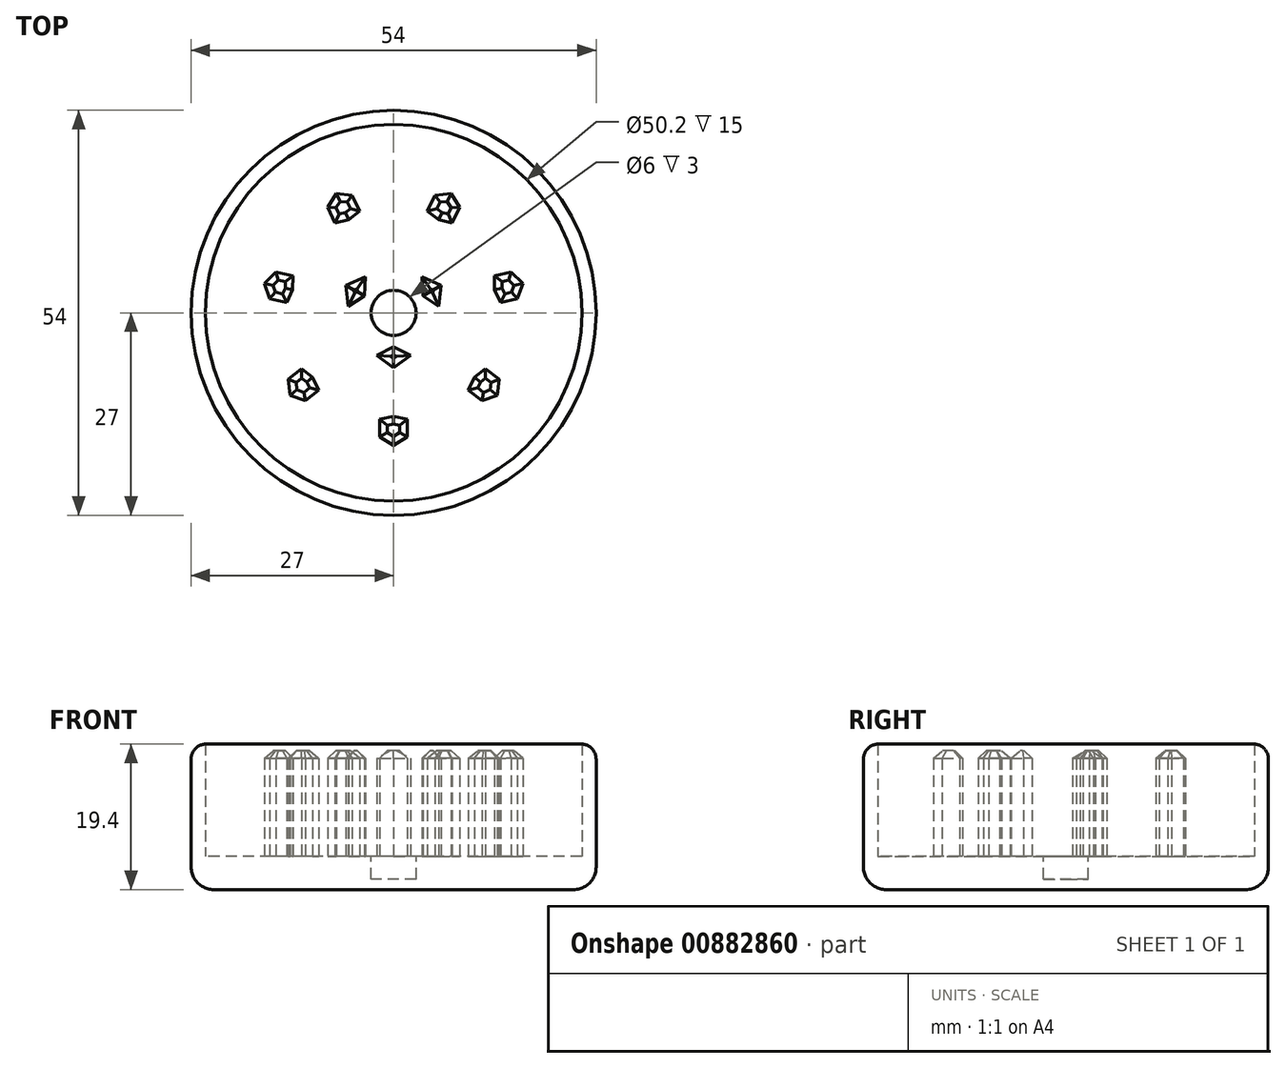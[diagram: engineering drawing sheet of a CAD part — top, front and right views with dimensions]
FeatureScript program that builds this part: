
annotation { "Feature Type Name" : "Feature", "Feature Type Description" : "" }
export const myFeature = defineFeature(function(context is Context, id is Id, definition is map)
    precondition{}
    {
        {
            var Q0;
            Q0=qCreatedBy(makeId("Top.planeOp"),FACE);
            var sketch = newSketch(context, id + "F0", { "sketchPlane" : qUnion([Q0])});
            skCircle(sketch, "E0", {"center": v(0, 0) * mm, "radius": 25 * mm});
            skCircle(sketch, "E1", {"center": v(0, 0) * mm, "radius": 27 * mm});
            skSolve(sketch);
        }
        {
            var Q0;
            Q0=makeQuery(id+"F0.imprint","IMPRINT",FACE,{"disambiguationData":[TD([[makeQuery(id+"F0.imprint","IMPRINT",EDGE,{"derivedFrom":sQuery(id+"F0.wireOp",EDGE,"E0")}),1.0]])]});
            extrude(context, id + "F1", {"entities" : qUnion([Q0]), "depth" : 4 * mm, "offsetDistance" : 25 * mm});
        }
        {
            var Q0;
            Q0=makeQuery(id+"F1.opExtrude","CAP_FACE",FACE,{"disambiguationData":[OSD([sQuery(id+"F0.wireOp",EDGE,"E0")])],"isStart":false});
            var sketch = newSketch(context, id + "F2", { "sketchPlane" : qUnion([Q0])});
            skCircle(sketch, "E2", {"center": v(0, 0) * mm, "radius": 25 * mm});
            skCircle(sketch, "E3", {"center": v(0, 0) * mm, "radius": 22 * mm});
            skCircle(sketch, "E4", {"center": v(0, 0) * mm, "radius": 4 * mm});
            skCircle(sketch, "E5", {"center": v(0, 0) * mm, "radius": 8 * mm});
            skCircle(sketch, "E6", {"center": v(0, 0) * mm, "radius": 13 * mm});
            skCircle(sketch, "E7", {"center": v(0, 0) * mm, "radius": 18 * mm});
            skLineSegment(sketch, "E8", {"start": v(0, 0) * mm, "end": v(0, -4) * mm});
            skLineSegment(sketch, "E9", {"start": v(0, -4) * mm, "end": v(4, 0) * mm});
            skLineSegment(sketch, "E10", {"start": v(4, 0) * mm, "end": v(0, 4) * mm});
            skLineSegment(sketch, "E11", {"start": v(0, 4) * mm, "end": v(-4, 0) * mm});
            skLineSegment(sketch, "E12", {"start": v(-4, 0) * mm, "end": v(0, -4) * mm});
            skLineSegment(sketch, "E13", {"start": v(0, -13) * mm, "end": v(-2.26, -10.11) * mm});
            skLineSegment(sketch, "E14", {"start": v(1.98, -10.11) * mm, "end": v(0, -13) * mm});
            skLineSegment(sketch, "E15", {"start": v(0, 18) * mm, "end": v(2.55, 21.85) * mm});
            skLineSegment(sketch, "E16", {"start": v(0, 18) * mm, "end": v(-2.55, 21.85) * mm});
            skLineSegment(sketch, "E17.1.0", {"start": v(-14.07, 11.22) * mm, "end": v(-18.67, 11.63) * mm});
            skLineSegment(sketch, "E17.1.1", {"start": v(-14.07, 11.22) * mm, "end": v(-15.5, 15.62) * mm});
            skLineSegment(sketch, "E17.2.0", {"start": v(-17.55, -4) * mm, "end": v(-20.74, -7.35) * mm});
            skLineSegment(sketch, "E17.2.1", {"start": v(-17.55, -4) * mm, "end": v(-21.87, -2.38) * mm});
            skLineSegment(sketch, "E17.3.0", {"start": v(-7.8, -16.22) * mm, "end": v(-7.19, -20.8) * mm});
            skLineSegment(sketch, "E17.3.1", {"start": v(-7.8, -16.22) * mm, "end": v(-11.78, -18.58) * mm});
            skLineSegment(sketch, "E17.4.0", {"start": v(7.8, -16.22) * mm, "end": v(11.78, -18.58) * mm});
            skLineSegment(sketch, "E17.4.1", {"start": v(7.8, -16.22) * mm, "end": v(7.19, -20.8) * mm});
            skLineSegment(sketch, "E17.5.0", {"start": v(17.55, -4) * mm, "end": v(21.87, -2.38) * mm});
            skLineSegment(sketch, "E17.5.1", {"start": v(17.55, -4) * mm, "end": v(20.74, -7.35) * mm});
            skLineSegment(sketch, "E17.6.0", {"start": v(14.07, 11.22) * mm, "end": v(15.5, 15.62) * mm});
            skLineSegment(sketch, "E17.6.1", {"start": v(14.07, 11.22) * mm, "end": v(18.67, 11.63) * mm});
            skLineSegment(sketch, "E18.1.0", {"start": v(10.11, -2.26) * mm, "end": v(8, 0) * mm});
            skLineSegment(sketch, "E18.1.2", {"start": v(8, 0) * mm, "end": v(10.11, 1.98) * mm});
            skLineSegment(sketch, "E18.2.0", {"start": v(2.26, 10.11) * mm, "end": v(0, 8) * mm});
            skLineSegment(sketch, "E18.2.1", {"start": v(-1.98, 10.11) * mm, "end": v(0, 13) * mm});
            skLineSegment(sketch, "E18.3.2", {"start": v(-8, 0) * mm, "end": v(-10.11, -1.98) * mm});
            skLineSegment(sketch, "E18.3.3", {"start": v(-13, 0) * mm, "end": v(-10.11, 2.26) * mm});
            skLineSegment(sketch, "E19", {"start": v(0, -13) * mm, "end": v(0, -13.8) * mm});
            skLineSegment(sketch, "E20", {"start": v(0, -13.8) * mm, "end": v(1.83, -14.2) * mm});
            skLineSegment(sketch, "E21", {"start": v(1.83, -14.2) * mm, "end": v(1.83, -16.51) * mm});
            skLineSegment(sketch, "E22", {"start": v(1.83, -16.51) * mm, "end": v(0, -17.67) * mm});
            skLineSegment(sketch, "E23.MirrorCS", {"start": v(0, -13.8) * mm, "end": v(-1.83, -14.2) * mm});
            skLineSegment(sketch, "E24.MirrorCS", {"start": v(-1.83, -14.2) * mm, "end": v(-1.83, -16.51) * mm});
            skLineSegment(sketch, "E25.MirrorCS", {"start": v(-1.83, -16.51) * mm, "end": v(0, -17.67) * mm});
            skLineSegment(sketch, "E26.1.0", {"start": v(9.97, -10.29) * mm, "end": v(11.77, -11.73) * mm});
            skLineSegment(sketch, "E26.1.1", {"start": v(10.79, -8.6) * mm, "end": v(9.97, -10.29) * mm});
            skLineSegment(sketch, "E26.1.2", {"start": v(10.79, -8.6) * mm, "end": v(12.25, -7.43) * mm});
            skLineSegment(sketch, "E26.1.3", {"start": v(12.25, -7.43) * mm, "end": v(14.05, -8.87) * mm});
            skLineSegment(sketch, "E26.1.4", {"start": v(14.05, -8.87) * mm, "end": v(13.81, -11.01) * mm});
            skLineSegment(sketch, "E26.1.5", {"start": v(11.77, -11.73) * mm, "end": v(13.81, -11.01) * mm});
            skLineSegment(sketch, "E26.2.0", {"start": v(14.26, 1.38) * mm, "end": v(16.5, 1.9) * mm});
            skLineSegment(sketch, "E26.2.1", {"start": v(13.45, 3.07) * mm, "end": v(14.26, 1.38) * mm});
            skLineSegment(sketch, "E26.2.2", {"start": v(13.45, 3.07) * mm, "end": v(13.44, 4.94) * mm});
            skLineSegment(sketch, "E26.2.3", {"start": v(13.44, 4.94) * mm, "end": v(15.7, 5.46) * mm});
            skLineSegment(sketch, "E26.2.4", {"start": v(15.7, 5.46) * mm, "end": v(17.22, 3.93) * mm});
            skLineSegment(sketch, "E26.2.5", {"start": v(16.5, 1.9) * mm, "end": v(17.22, 3.93) * mm});
            skLineSegment(sketch, "E26.3.0", {"start": v(7.81, 12) * mm, "end": v(8.81, 14.08) * mm});
            skLineSegment(sketch, "E26.3.1", {"start": v(5.99, 12.43) * mm, "end": v(7.81, 12) * mm});
            skLineSegment(sketch, "E26.3.2", {"start": v(5.99, 12.43) * mm, "end": v(4.52, 13.6) * mm});
            skLineSegment(sketch, "E26.3.3", {"start": v(4.52, 13.6) * mm, "end": v(5.52, 15.67) * mm});
            skLineSegment(sketch, "E26.3.4", {"start": v(5.52, 15.67) * mm, "end": v(7.67, 15.92) * mm});
            skLineSegment(sketch, "E26.3.5", {"start": v(8.81, 14.08) * mm, "end": v(7.67, 15.92) * mm});
            skLineSegment(sketch, "E26.4.0", {"start": v(-4.52, 13.6) * mm, "end": v(-5.52, 15.67) * mm});
            skLineSegment(sketch, "E26.4.1", {"start": v(-5.99, 12.43) * mm, "end": v(-4.52, 13.6) * mm});
            skLineSegment(sketch, "E26.4.2", {"start": v(-5.99, 12.43) * mm, "end": v(-7.81, 12) * mm});
            skLineSegment(sketch, "E26.4.3", {"start": v(-7.81, 12) * mm, "end": v(-8.81, 14.08) * mm});
            skLineSegment(sketch, "E26.4.4", {"start": v(-8.81, 14.08) * mm, "end": v(-7.67, 15.92) * mm});
            skLineSegment(sketch, "E26.4.5", {"start": v(-5.52, 15.67) * mm, "end": v(-7.67, 15.92) * mm});
            skLineSegment(sketch, "E26.5.0", {"start": v(-13.44, 4.94) * mm, "end": v(-15.7, 5.46) * mm});
            skLineSegment(sketch, "E26.5.1", {"start": v(-13.45, 3.07) * mm, "end": v(-13.44, 4.94) * mm});
            skLineSegment(sketch, "E26.5.2", {"start": v(-13.45, 3.07) * mm, "end": v(-14.26, 1.38) * mm});
            skLineSegment(sketch, "E26.5.3", {"start": v(-14.26, 1.38) * mm, "end": v(-16.5, 1.9) * mm});
            skLineSegment(sketch, "E26.5.4", {"start": v(-16.5, 1.9) * mm, "end": v(-17.22, 3.93) * mm});
            skLineSegment(sketch, "E26.5.5", {"start": v(-15.7, 5.46) * mm, "end": v(-17.22, 3.93) * mm});
            skLineSegment(sketch, "E26.6.0", {"start": v(-12.25, -7.43) * mm, "end": v(-14.05, -8.87) * mm});
            skLineSegment(sketch, "E26.6.1", {"start": v(-10.79, -8.6) * mm, "end": v(-12.25, -7.43) * mm});
            skLineSegment(sketch, "E26.6.2", {"start": v(-10.79, -8.6) * mm, "end": v(-9.97, -10.29) * mm});
            skLineSegment(sketch, "E26.6.3", {"start": v(-9.97, -10.29) * mm, "end": v(-11.77, -11.73) * mm});
            skLineSegment(sketch, "E26.6.4", {"start": v(-11.77, -11.73) * mm, "end": v(-13.81, -11.01) * mm});
            skLineSegment(sketch, "E26.6.5", {"start": v(-14.05, -8.87) * mm, "end": v(-13.81, -11.01) * mm});
            skLineSegment(sketch, "E27", {"start": v(0, -4.5) * mm, "end": v(2.26, -5.67) * mm});
            skLineSegment(sketch, "E28", {"start": v(2.26, -5.67) * mm, "end": v(0, -7.34) * mm});
            skLineSegment(sketch, "E29.MirrorCS", {"start": v(0, -4.5) * mm, "end": v(-2.26, -5.67) * mm});
            skLineSegment(sketch, "E30.MirrorCS", {"start": v(-2.26, -5.67) * mm, "end": v(0, -7.34) * mm});
            skLineSegment(sketch, "E31.1.0", {"start": v(3.9, 2.25) * mm, "end": v(6.05, 0.88) * mm});
            skLineSegment(sketch, "E31.1.1", {"start": v(6.05, 0.88) * mm, "end": v(6.36, 3.67) * mm});
            skLineSegment(sketch, "E31.1.2", {"start": v(3.78, 4.8) * mm, "end": v(6.36, 3.67) * mm});
            skLineSegment(sketch, "E31.1.3", {"start": v(3.9, 2.25) * mm, "end": v(3.78, 4.8) * mm});
            skLineSegment(sketch, "E31.2.0", {"start": v(-3.9, 2.25) * mm, "end": v(-3.78, 4.8) * mm});
            skLineSegment(sketch, "E31.2.1", {"start": v(-3.78, 4.8) * mm, "end": v(-6.36, 3.67) * mm});
            skLineSegment(sketch, "E31.2.2", {"start": v(-6.05, 0.88) * mm, "end": v(-6.36, 3.67) * mm});
            skLineSegment(sketch, "E31.2.3", {"start": v(-3.9, 2.25) * mm, "end": v(-6.05, 0.88) * mm});
            skCircle(sketch, "E32", {"center": v(0, 0) * mm, "radius": 27 * mm});
            skSolve(sketch);
        }
        {
            var Q0;
            Q0=makeQuery(id+"F1.opExtrude","CAP_FACE",FACE,{"disambiguationData":[OSD([sQuery(id+"F0.wireOp",EDGE,"E0")])],"isStart":true});
            var sketch = newSketch(context, id + "F3", { "sketchPlane" : qUnion([Q0])});
            skCircle(sketch, "E33", {"center": v(0, 0) * mm, "radius": 27 * mm});
            skSolve(sketch);
        }
        {
            var Q0;
            Q0 = qSketchRegion(id + "F3", true);
            extrude(context, id + "F4", {"entities" : qUnion([Q0]), "operationType" : NewBodyOperationType.ADD, "oppositeDirection" : true, "depth" : 4.4 * mm, "offsetDistance" : 25 * mm});
        }
        {
            var Q0;
            Q0=makeQuery(id+"F2.imprint","IMPRINT",FACE,{"disambiguationData":[TD([[makeQuery(id+"F2.imprint","IMPRINT",EDGE,{"derivedFrom":sQuery(id+"F2.wireOp",EDGE,"E31.1.0")}),1.0]])]});
            var Q1;
            Q1=makeQuery(id+"F2.imprint","IMPRINT",FACE,{"disambiguationData":[TD([[makeQuery(id+"F2.imprint","IMPRINT",EDGE,{"derivedFrom":sQuery(id+"F2.wireOp",EDGE,"E31.2.0")}),1.0]])]});
            var Q2;
            Q2=makeQuery(id+"F2.imprint","IMPRINT",FACE,{"disambiguationData":[TD([[makeQuery(id+"F2.imprint","IMPRINT",EDGE,{"derivedFrom":sQuery(id+"F2.wireOp",EDGE,"E27")}),-1.0]])]});
            var Q3;
            Q3=makeQuery(id+"F2.imprint","IMPRINT",FACE,{"disambiguationData":[TD([[makeQuery(id+"F2.imprint","IMPRINT",EDGE,{"derivedFrom":sQuery(id+"F2.wireOp",EDGE,"E18.2.0")}),-1.0]])]});
            var Q4;
            Q4=makeQuery(id+"F2.imprint","IMPRINT",FACE,{"disambiguationData":[TD([[makeQuery(id+"F2.imprint","IMPRINT",EDGE,{"derivedFrom":sQuery(id+"F2.wireOp",EDGE,"E18.3.0")}),-1.0]])]});
            var Q5;
            Q5=makeQuery(id+"F2.imprint","IMPRINT",FACE,{"disambiguationData":[TD([[makeQuery(id+"F2.imprint","IMPRINT",EDGE,{"derivedFrom":sQuery(id+"F2.wireOp",EDGE,"E13")}),-1.0]])]});
            var Q6;
            Q6=makeQuery(id+"F2.imprint","IMPRINT",FACE,{"disambiguationData":[TD([[makeQuery(id+"F2.imprint","IMPRINT",EDGE,{"derivedFrom":sQuery(id+"F2.wireOp",EDGE,"E18.1.0")}),-1.0]])]});
            var Q7;
            Q7=makeQuery(id+"F2.imprint","IMPRINT",FACE,{"disambiguationData":[TD([[makeQuery(id+"F2.imprint","IMPRINT",EDGE,{"derivedFrom":sQuery(id+"F2.wireOp",EDGE,"E26.4.0")}),1.0]])]});
            var Q8;
            Q8=makeQuery(id+"F2.imprint","IMPRINT",FACE,{"disambiguationData":[TD([[makeQuery(id+"F2.imprint","IMPRINT",EDGE,{"derivedFrom":sQuery(id+"F2.wireOp",EDGE,"E26.3.0")}),1.0]])]});
            var Q9;
            Q9=makeQuery(id+"F2.imprint","IMPRINT",FACE,{"disambiguationData":[TD([[makeQuery(id+"F2.imprint","IMPRINT",EDGE,{"derivedFrom":sQuery(id+"F2.wireOp",EDGE,"E26.2.0")}),1.0]])]});
            var Q10;
            Q10=makeQuery(id+"F2.imprint","IMPRINT",FACE,{"disambiguationData":[TD([[makeQuery(id+"F2.imprint","IMPRINT",EDGE,{"derivedFrom":sQuery(id+"F2.wireOp",EDGE,"E26.1.0")}),1.0]])]});
            var Q11;
            Q11=makeQuery(id+"F2.imprint","IMPRINT",FACE,{"disambiguationData":[TD([[makeQuery(id+"F2.imprint","IMPRINT",EDGE,{"derivedFrom":sQuery(id+"F2.wireOp",EDGE,"E20")}),-1.0]])]});
            var Q12;
            Q12=makeQuery(id+"F2.imprint","IMPRINT",FACE,{"disambiguationData":[TD([[makeQuery(id+"F2.imprint","IMPRINT",EDGE,{"derivedFrom":sQuery(id+"F2.wireOp",EDGE,"E26.6.0")}),1.0]])]});
            var Q13;
            Q13=makeQuery(id+"F2.imprint","IMPRINT",FACE,{"disambiguationData":[TD([[makeQuery(id+"F2.imprint","IMPRINT",EDGE,{"derivedFrom":sQuery(id+"F2.wireOp",EDGE,"E26.5.0")}),1.0]])]});
            extrude(context, id + "F5", {"entities" : qUnion([Q0, Q1, Q2, Q3, Q4, Q5, Q6, Q7, Q8, Q9, Q10, Q11, Q12, Q13]), "operationType" : NewBodyOperationType.ADD, "depth" : 14.5 * mm, "offsetDistance" : 25 * mm});
        }
        {
            var Q0;
            Q0=makeQuery(id+"F4.opExtrude","CAP_FACE",FACE,{"disambiguationData":[OSD([sQuery(id+"F3.wireOp",EDGE,"E33")])],"isStart":false});
            var sketch = newSketch(context, id + "F6", { "sketchPlane" : qUnion([Q0])});
            skCircle(sketch, "E34", {"center": v(0, 0) * mm, "radius": 25.1 * mm});
            skCircle(sketch, "E35", {"center": v(0, 0) * mm, "radius": 27 * mm});
            skSolve(sketch);
        }
        {
            var Q0;
            Q0 = qSketchRegion(id + "F6", true);
            extrude(context, id + "F7", {"entities" : qUnion([Q0]), "operationType" : NewBodyOperationType.ADD, "depth" : 15 * mm, "offsetDistance" : 25 * mm});
        }
        {
            var Q0;
            Q0=makeQuery(id+"F7.opExtrude","CAP_EDGE",EDGE,{"disambiguationData":[OSD([sQuery(id+"F6.wireOp",EDGE,"E35")])],"isStart":false});
            fillet(context, id + "F8", {"entities" : qUnion([Q0]), "radius" : 2 * mm, "tangentPropagation" : true, "allowEdgeOverflow" : false});
        }
        {
            var Q0;
            Q0=makeQuery(id+"F4.boolean.opBoolean","MERGE",FACE,{"derivedFrom":[makeQuery(id+"F1.opExtrude","CAP_FACE",FACE,{"disambiguationData":[OSD([sQuery(id+"F0.wireOp",EDGE,"E0")])],"isStart":true}),makeQuery(id+"F4.opExtrude","CAP_FACE",FACE,{"disambiguationData":[OSD([sQuery(id+"F3.wireOp",EDGE,"E33")])],"isStart":true})]});
            fillet(context, id + "F9", {"entities" : qUnion([Q0]), "radius" : 3 * mm, "tangentPropagation" : true, "allowEdgeOverflow" : false});
        }
        {
            var Q0;
            Q0=makeQuery(id+"F5.opExtrude","CAP_FACE",FACE,{"disambiguationData":[OSD([sQuery(id+"F2.wireOp",EDGE,"E27"),sQuery(id+"F2.wireOp",EDGE,"E28"),sQuery(id+"F2.wireOp",EDGE,"E29.MirrorCS"),sQuery(id+"F2.wireOp",EDGE,"E30.MirrorCS")])],"isStart":false});
            var Q1;
            Q1=makeQuery(id+"F5.opExtrude","CAP_FACE",FACE,{"disambiguationData":[OSD([sQuery(id+"F2.wireOp",EDGE,"E31.1.0"),sQuery(id+"F2.wireOp",EDGE,"E31.1.1"),sQuery(id+"F2.wireOp",EDGE,"E31.1.2"),sQuery(id+"F2.wireOp",EDGE,"E31.1.3")])],"isStart":false});
            var Q2;
            Q2=makeQuery(id+"F5.opExtrude","CAP_FACE",FACE,{"disambiguationData":[OSD([sQuery(id+"F2.wireOp",EDGE,"E26.3.0"),sQuery(id+"F2.wireOp",EDGE,"E26.3.1"),sQuery(id+"F2.wireOp",EDGE,"E26.3.2"),sQuery(id+"F2.wireOp",EDGE,"E26.3.3"),sQuery(id+"F2.wireOp",EDGE,"E26.3.4"),sQuery(id+"F2.wireOp",EDGE,"E26.3.5")])],"isStart":false});
            var Q3;
            Q3=makeQuery(id+"F5.opExtrude","CAP_FACE",FACE,{"disambiguationData":[OSD([sQuery(id+"F2.wireOp",EDGE,"E31.2.0"),sQuery(id+"F2.wireOp",EDGE,"E31.2.1"),sQuery(id+"F2.wireOp",EDGE,"E31.2.2"),sQuery(id+"F2.wireOp",EDGE,"E31.2.3")])],"isStart":false});
            var Q4;
            Q4=makeQuery(id+"F5.opExtrude","CAP_FACE",FACE,{"disambiguationData":[OSD([sQuery(id+"F2.wireOp",EDGE,"E26.4.0"),sQuery(id+"F2.wireOp",EDGE,"E26.4.1"),sQuery(id+"F2.wireOp",EDGE,"E26.4.2"),sQuery(id+"F2.wireOp",EDGE,"E26.4.3"),sQuery(id+"F2.wireOp",EDGE,"E26.4.4"),sQuery(id+"F2.wireOp",EDGE,"E26.4.5")])],"isStart":false});
            var Q5;
            Q5=makeQuery(id+"F5.opExtrude","CAP_FACE",FACE,{"disambiguationData":[OSD([sQuery(id+"F2.wireOp",EDGE,"E26.2.0"),sQuery(id+"F2.wireOp",EDGE,"E26.2.1"),sQuery(id+"F2.wireOp",EDGE,"E26.2.2"),sQuery(id+"F2.wireOp",EDGE,"E26.2.3"),sQuery(id+"F2.wireOp",EDGE,"E26.2.4"),sQuery(id+"F2.wireOp",EDGE,"E26.2.5")])],"isStart":false});
            var Q6;
            Q6=makeQuery(id+"F5.opExtrude","CAP_FACE",FACE,{"disambiguationData":[OSD([sQuery(id+"F2.wireOp",EDGE,"E26.1.0"),sQuery(id+"F2.wireOp",EDGE,"E26.1.1"),sQuery(id+"F2.wireOp",EDGE,"E26.1.2"),sQuery(id+"F2.wireOp",EDGE,"E26.1.3"),sQuery(id+"F2.wireOp",EDGE,"E26.1.4"),sQuery(id+"F2.wireOp",EDGE,"E26.1.5")])],"isStart":false});
            var Q7;
            Q7=makeQuery(id+"F5.opExtrude","CAP_FACE",FACE,{"disambiguationData":[OSD([sQuery(id+"F2.wireOp",EDGE,"E20"),sQuery(id+"F2.wireOp",EDGE,"E21"),sQuery(id+"F2.wireOp",EDGE,"E22"),sQuery(id+"F2.wireOp",EDGE,"E23.MirrorCS"),sQuery(id+"F2.wireOp",EDGE,"E24.MirrorCS"),sQuery(id+"F2.wireOp",EDGE,"E25.MirrorCS")])],"isStart":false});
            var Q8;
            Q8=makeQuery(id+"F5.opExtrude","CAP_FACE",FACE,{"disambiguationData":[OSD([sQuery(id+"F2.wireOp",EDGE,"E26.6.0"),sQuery(id+"F2.wireOp",EDGE,"E26.6.1"),sQuery(id+"F2.wireOp",EDGE,"E26.6.2"),sQuery(id+"F2.wireOp",EDGE,"E26.6.3"),sQuery(id+"F2.wireOp",EDGE,"E26.6.4"),sQuery(id+"F2.wireOp",EDGE,"E26.6.5")])],"isStart":false});
            var Q9;
            Q9=makeQuery(id+"F5.opExtrude","CAP_FACE",FACE,{"disambiguationData":[OSD([sQuery(id+"F2.wireOp",EDGE,"E26.5.0"),sQuery(id+"F2.wireOp",EDGE,"E26.5.1"),sQuery(id+"F2.wireOp",EDGE,"E26.5.2"),sQuery(id+"F2.wireOp",EDGE,"E26.5.3"),sQuery(id+"F2.wireOp",EDGE,"E26.5.4"),sQuery(id+"F2.wireOp",EDGE,"E26.5.5")])],"isStart":false});
            chamfer(context, id + "F10", {"entities" : qUnion([Q0, Q1, Q2, Q3, Q4, Q5, Q6, Q7, Q8, Q9]), "width" : (1) * mm, "tangentPropagation" : true});
        }
        {
            var Q0;
            Q0=makeQuery(id+"F4.opExtrude","CAP_FACE",FACE,{"disambiguationData":[OSD([sQuery(id+"F3.wireOp",EDGE,"E33")])],"isStart":false});
            var sketch = newSketch(context, id + "F11", { "sketchPlane" : qUnion([Q0])});
            skCircle(sketch, "E36", {"center": v(0, 0) * mm, "radius": 3 * mm});
            skSolve(sketch);
        }
        {
            var Q0;
            Q0 = qSketchRegion(id + "F11", true);
            extrude(context, id + "F12", {"entities" : qUnion([Q0]), "operationType" : NewBodyOperationType.REMOVE, "oppositeDirection" : true, "depth" : 3 * mm, "offsetDistance" : 25 * mm});
        }
    });
